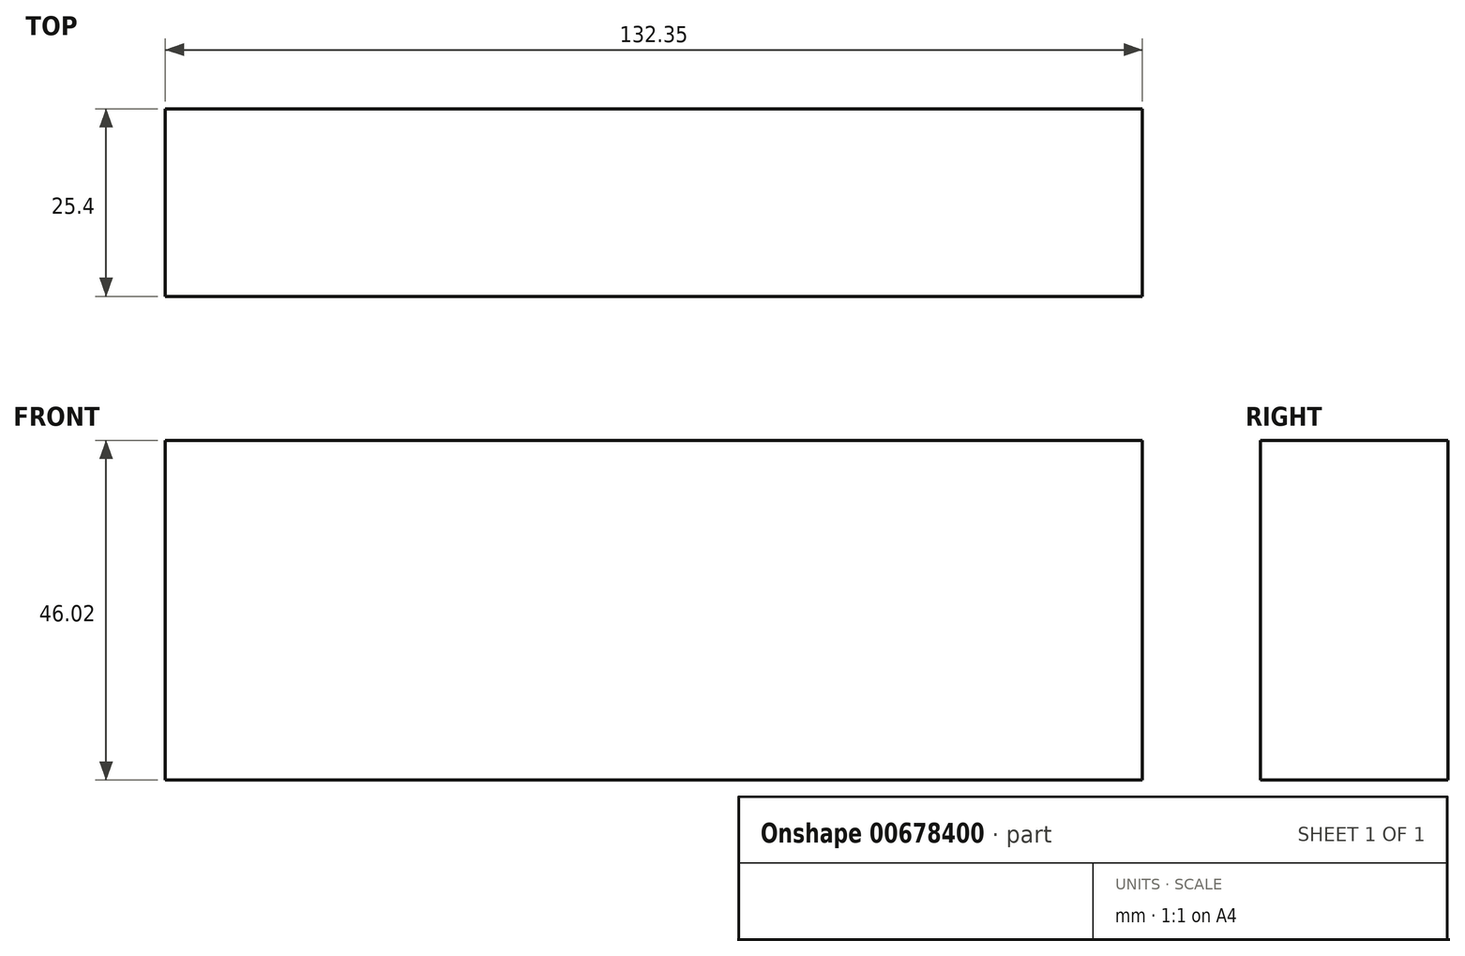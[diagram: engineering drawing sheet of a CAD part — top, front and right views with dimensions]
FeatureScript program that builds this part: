
annotation { "Feature Type Name" : "Feature", "Feature Type Description" : "" }
export const myFeature = defineFeature(function(context is Context, id is Id, definition is map)
    precondition{}
    {
        {
            var Q0;
            Q0=qCreatedBy(makeId("Front.planeOp"),FACE);
            var sketch = newSketch(context, id + "F0", { "sketchPlane" : qUnion([Q0])});
            skCircle(sketch, "E0", {"center": v(-41.36, 39.25) * mm, "radius": 18.43 * mm});
            skLineSegment(sketch, "E1.bottom", {"start": v(-65.12, 61.51) * mm, "end": v(67.23, 61.51) * mm});
            skLineSegment(sketch, "E1.top", {"start": v(-65.12, 15.5) * mm, "end": v(67.23, 15.5) * mm});
            skLineSegment(sketch, "E1.left", {"start": v(-65.12, 61.51) * mm, "end": v(-65.12, 15.5) * mm});
            skLineSegment(sketch, "E1.right", {"start": v(67.23, 61.51) * mm, "end": v(67.23, 15.5) * mm});
            skSolve(sketch);
        }
        {
            var Q0;
            Q0=makeQuery(id+"F0.imprint","IMPRINT",FACE,{"disambiguationData":[TD([[makeQuery(id+"F0.imprint","IMPRINT",EDGE,{"derivedFrom":sQuery(id+"F0.wireOp",EDGE,"E0")}),1.0]])]});
            extrude(context, id + "F1", {"entities" : qUnion([Q0]), "depth" : 25.4 * mm, "offsetDistance" : 25.4 * mm});
        }
        {
            var Q0;
            Q0=makeQuery(id+"F0.imprint","IMPRINT",FACE,{"disambiguationData":[TD([[makeQuery(id+"F0.imprint","IMPRINT",EDGE,{"derivedFrom":sQuery(id+"F0.wireOp",EDGE,"E0")}),-1.0]])]});
            extrude(context, id + "F2", {"entities" : qUnion([Q0]), "operationType" : NewBodyOperationType.ADD, "depth" : 25.4 * mm, "offsetDistance" : 25.4 * mm});
        }
    });
